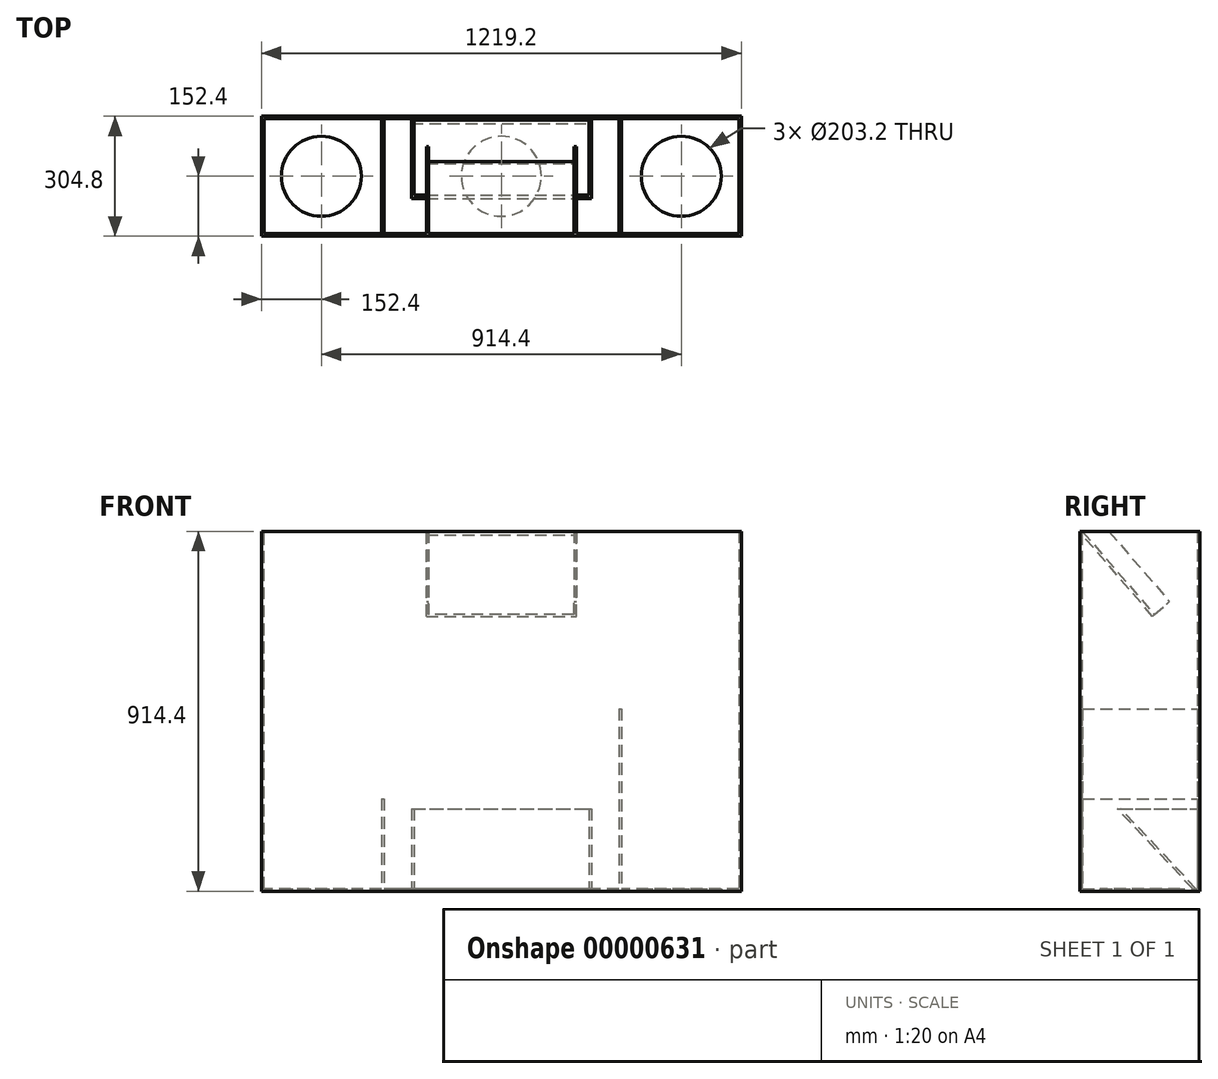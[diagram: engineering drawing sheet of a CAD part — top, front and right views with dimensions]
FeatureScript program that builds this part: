
annotation { "Feature Type Name" : "Feature", "Feature Type Description" : "" }
export const myFeature = defineFeature(function(context is Context, id is Id, definition is map)
    precondition{}
    {
        {
            var Q0;
            Q0=qCreatedBy(makeId("Front.planeOp"),FACE);
            var sketch = newSketch(context, id + "F0", { "sketchPlane" : qUnion([Q0])});
            skLineSegment(sketch, "E0", {"start": v(0, 0) * mm, "end": v(0, 914.4) * mm});
            skLineSegment(sketch, "E1", {"start": v(0, 914.4) * mm, "end": v(1219.2, 914.4) * mm});
            skLineSegment(sketch, "E2", {"start": v(1219.2, 914.4) * mm, "end": v(1219.2, 0) * mm});
            skLineSegment(sketch, "E3", {"start": v(1219.2, 0) * mm, "end": v(0, 0) * mm});
            skSolve(sketch);
        }
        {
            var Q0;
            Q0=makeQuery(id+"F0.imprint","IMPRINT",FACE,{"disambiguationData":[TD([[makeQuery(id+"F0.imprint","IMPRINT",EDGE,{"derivedFrom":sQuery(id+"F0.wireOp",EDGE,"E0")}),-1.0]])]});
            extrude(context, id + "F1", {"entities" : qUnion([Q0]), "depth" : 304.8 * mm});
        }
        {
            var Q0;
            Q0=sQuery(id+"F0.wireOp",EDGE,"E3");
            cPlane(context, id + "F2", {"entities" : qUnion([Q0]), "cplaneType" : CPlaneType.MID_PLANE, "offset" : 152.4 * mm, "width" : 152.4 * mm, "height" : 152.4 * mm});
        }
        {
            var Q0;
            Q0=makeQuery(id+"F1.opExtrude","SWEPT_FACE",FACE,{"disambiguationData":[OSD([sQuery(id+"F0.wireOp",EDGE,"E1")])]});
            shell(context, id + "F3", {"entities" : qUnion([Q0]), "thickness" : 6.35 * mm});
        }
        {
            var Q0;
            Q0=makeQuery(id+"F1.opExtrude","SWEPT_FACE",FACE,{"disambiguationData":[OSD([sQuery(id+"F0.wireOp",EDGE,"E3")])]});
            var sketch = newSketch(context, id + "F4", { "sketchPlane" : qUnion([Q0])});
            skLineSegment(sketch, "E4.0", {"start": v(0, 304.8) * mm, "end": v(0, 0) * mm});
            skLineSegment(sketch, "E4.1", {"start": v(1219.2, 304.8) * mm, "end": v(0, 304.8) * mm});
            skLineSegment(sketch, "E4.2", {"start": v(1219.2, 304.8) * mm, "end": v(1219.2, 0) * mm});
            skLineSegment(sketch, "E4.3", {"start": v(1219.2, 0) * mm, "end": v(0, 0) * mm});
            skLineSegment(sketch, "E5", {"start": v(0, 152.4) * mm, "end": v(1219.2, 152.4) * mm, "construction": true});
            skCircle(sketch, "E6", {"center": v(609.6, 152.4) * mm, "radius": 101.6 * mm});
            skCircle(sketch, "E7", {"center": v(1066.8, 152.4) * mm, "radius": 101.6 * mm});
            skCircle(sketch, "E8", {"center": v(152.4, 152.4) * mm, "radius": 101.6 * mm});
            skLineSegment(sketch, "E9", {"start": v(304.8, 304.8) * mm, "end": v(304.8, 0) * mm});
            skLineSegment(sketch, "E10", {"start": v(311.15, 304.8) * mm, "end": v(311.15, 0) * mm});
            skLineSegment(sketch, "E11", {"start": v(914.4, 304.8) * mm, "end": v(914.4, 0) * mm});
            skLineSegment(sketch, "E12", {"start": v(908.05, 304.8) * mm, "end": v(908.05, 0) * mm});
            skSolve(sketch);
        }
        {
            var Q0;
            Q0=makeQuery(id+"F4.imprint","IMPRINT",FACE,{"disambiguationData":[TD([[makeQuery(id+"F4.imprint","IMPRINT",EDGE,{"derivedFrom":sQuery(id+"F4.wireOp",EDGE,"E8")}),1.0]])]});
            var Q1;
            Q1=makeQuery(id+"F4.imprint","IMPRINT",FACE,{"disambiguationData":[TD([[makeQuery(id+"F4.imprint","IMPRINT",EDGE,{"derivedFrom":sQuery(id+"F4.wireOp",EDGE,"E6")}),1.0]])]});
            var Q2;
            Q2=makeQuery(id+"F4.imprint","IMPRINT",FACE,{"disambiguationData":[TD([[makeQuery(id+"F4.imprint","IMPRINT",EDGE,{"derivedFrom":sQuery(id+"F4.wireOp",EDGE,"E7")}),1.0]])]});
            var Q3;
            Q3=makeQuery(id+"F3.opShell","OFFSET_FACE",FACE,{"disambiguationData":[OSD([sQuery(id+"F0.wireOp",EDGE,"E3")])]});
            extrude(context, id + "F5", {"entities" : qUnion([Q0, Q1, Q2]), "operationType" : NewBodyOperationType.REMOVE, "endBound" : BoundingType.UP_TO_SURFACE, "oppositeDirection" : true, "endBoundEntityFace" : qUnion([Q3]), "depth" : 25.4 * mm});
        }
        {
            var Q0;
            Q0=qCreatedBy(id+"F2.planeOp",FACE);
            var sketch = newSketch(context, id + "F6", { "sketchPlane" : qUnion([Q0])});
            skLineSegment(sketch, "E13", {"start": v(12.7, 0) * mm, "end": v(209.55, 209.55) * mm});
            skLineSegment(sketch, "E14", {"start": v(209.55, 209.55) * mm, "end": v(0, 209.55) * mm});
            skLineSegment(sketch, "E15.0", {"start": v(0, 0) * mm, "end": v(0, 914.4) * mm});
            skLineSegment(sketch, "E16.0", {"start": v(304.8, 0) * mm, "end": v(0, 0) * mm});
            skSolve(sketch);
        }
        {
            var Q0;
            {var subQ3=sQuery(id+"F6.wireOp",EDGE,"E13");Q0=makeQuery(id+"F6.imprint","IMPRINT",FACE,{"disambiguationData":[TD([[makeQuery(id+"F6.imprint","IMPRINT",EDGE,{"derivedFrom":subQ3}),1.0]])]});}
            extrude(context, id + "F7", {"entities" : qUnion([Q0]), "operationType" : NewBodyOperationType.ADD, "endBound" : BoundingType.SYMMETRIC, "depth" : 457.2 * mm});
        }
        {
            var Q0;
            Q0=makeQuery(id+"F7.opExtrude","SWEPT_FACE",FACE,{"disambiguationData":[OSD([sQuery(id+"F6.wireOp",EDGE,"E14")])]});
            shell(context, id + "F8", {"entities" : qUnion([Q0]), "thickness" : 6.35 * mm});
        }
        {
            var Q0;
            Q0=qCreatedBy(id+"F2.planeOp",FACE);
            var sketch = newSketch(context, id + "F9", { "sketchPlane" : qUnion([Q0])});
            skLineSegment(sketch, "E17.0", {"start": v(298.45, 6.35) * mm, "end": v(298.45, 914.4) * mm});
            skLineSegment(sketch, "E18", {"start": v(298.45, 914.4) * mm, "end": v(115.84, 702.93) * mm});
            skLineSegment(sketch, "E19", {"start": v(120.65, 698.78) * mm, "end": v(298.45, 904.68) * mm});
            skLineSegment(sketch, "E20", {"start": v(231.33, 914.4) * mm, "end": v(77.4, 736.13) * mm});
            skLineSegment(sketch, "E21", {"start": v(120.65, 698.78) * mm, "end": v(77.4, 736.13) * mm});
            skLineSegment(sketch, "E22.0", {"start": v(304.8, 914.4) * mm, "end": v(0, 914.4) * mm});
            skLineSegment(sketch, "E23.0", {"start": v(0, 0) * mm, "end": v(0, 920.75) * mm});
            skLineSegment(sketch, "E23.1", {"start": v(304.8, 0) * mm, "end": v(304.8, 920.75) * mm});
            skLineSegment(sketch, "E24", {"start": v(0, 920.75) * mm, "end": v(304.8, 920.75) * mm});
            skSolve(sketch);
        }
        {
            var Q0;
            {var subQ2=sQuery(id+"F9.wireOp",EDGE,"E18");Q0=makeQuery(id+"F9.imprint","IMPRINT",FACE,{"disambiguationData":[TD([[makeQuery(id+"F9.imprint","IMPRINT",EDGE,{"derivedFrom":subQ2}),1.0]])]});}
            var Q1;
            {var subQ2=sQuery(id+"F9.wireOp",EDGE,"E18");Q1=makeQuery(id+"F9.imprint","IMPRINT",FACE,{"disambiguationData":[TD([[makeQuery(id+"F9.imprint","IMPRINT",EDGE,{"derivedFrom":subQ2}),-1.0]])]});}
            extrude(context, id + "F10", {"entities" : qUnion([Q0, Q1]), "operationType" : NewBodyOperationType.ADD, "endBound" : BoundingType.SYMMETRIC, "depth" : 381 * mm});
        }
        {
            var Q0;
            {var subQ2=sQuery(id+"F9.wireOp",EDGE,"E18");Q0=makeQuery(id+"F9.imprint","IMPRINT",FACE,{"disambiguationData":[TD([[makeQuery(id+"F9.imprint","IMPRINT",EDGE,{"derivedFrom":subQ2}),-1.0]])]});}
            extrude(context, id + "F11", {"entities" : qUnion([Q0]), "operationType" : NewBodyOperationType.REMOVE, "endBound" : BoundingType.SYMMETRIC, "oppositeDirection" : true, "depth" : 368.3 * mm});
        }
        {
            var Q0;
            {var subQ1=sQuery(id+"F4.wireOp",EDGE,"E11");Q0=makeQuery(id+"F4.imprint","IMPRINT",FACE,{"disambiguationData":[TD([[makeQuery(id+"F4.imprint","IMPRINT",EDGE,{"derivedFrom":subQ1}),-1.0]])]});}
            extrude(context, id + "F12", {"entities" : qUnion([Q0]), "operationType" : NewBodyOperationType.ADD, "oppositeDirection" : true, "depth" : 463.55 * mm});
        }
        {
            var Q0;
            {var subQ1=sQuery(id+"F4.wireOp",EDGE,"E9");Q0=makeQuery(id+"F4.imprint","IMPRINT",FACE,{"disambiguationData":[TD([[makeQuery(id+"F4.imprint","IMPRINT",EDGE,{"derivedFrom":subQ1}),1.0]])]});}
            extrude(context, id + "F13", {"entities" : qUnion([Q0]), "operationType" : NewBodyOperationType.ADD, "oppositeDirection" : true, "depth" : 234.95 * mm});
        }
    });
